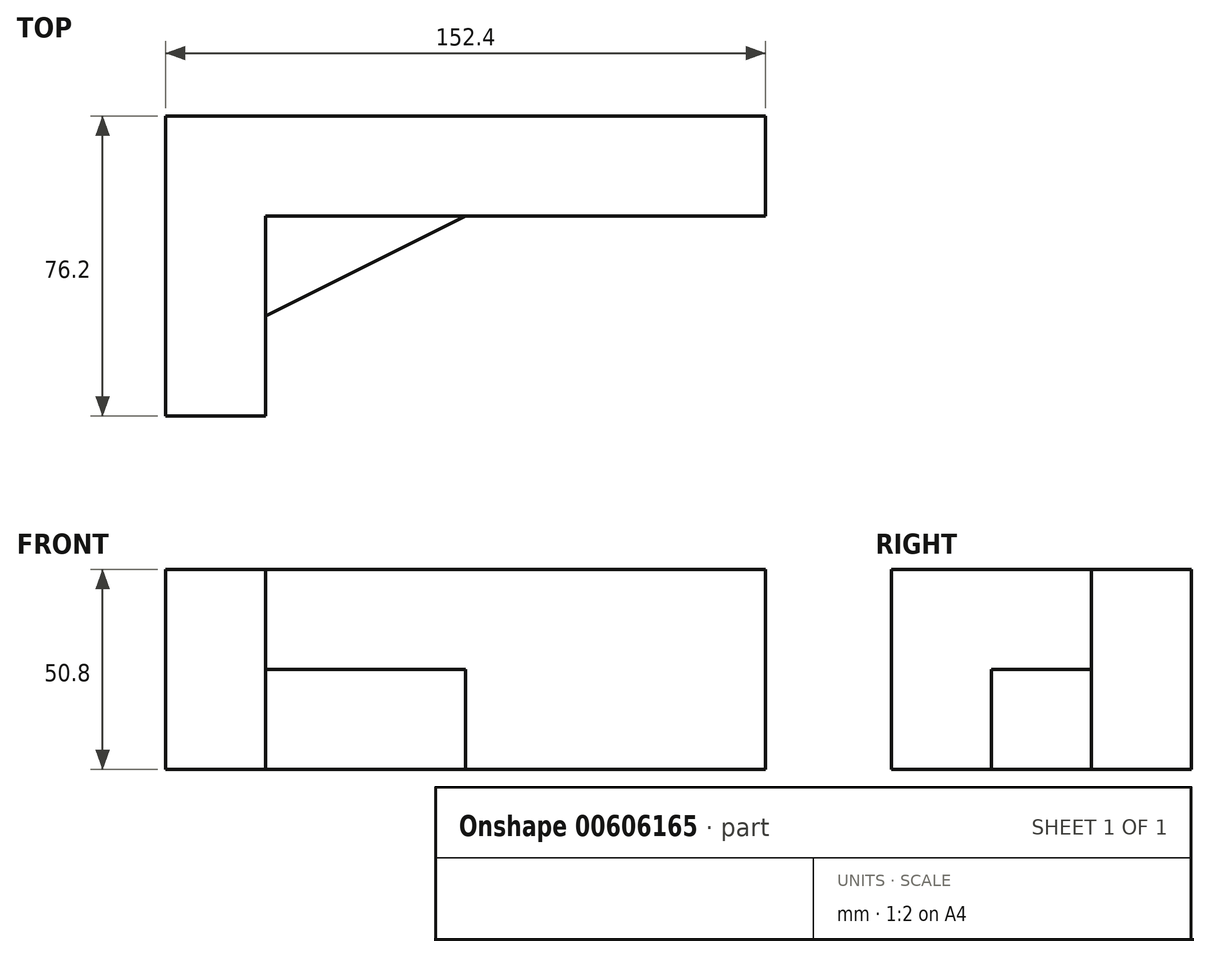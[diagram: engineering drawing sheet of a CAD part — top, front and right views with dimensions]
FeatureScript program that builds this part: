
annotation { "Feature Type Name" : "Feature", "Feature Type Description" : "" }
export const myFeature = defineFeature(function(context is Context, id is Id, definition is map)
    precondition{}
    {
        {
            var Q0;
            Q0=qCreatedBy(makeId("Top.planeOp"),FACE);
            var sketch = newSketch(context, id + "F0", { "sketchPlane" : qUnion([Q0])});
            skLineSegment(sketch, "E0", {"start": v(-46.57, 0) * mm, "end": v(-46.57, 76.2) * mm});
            skLineSegment(sketch, "E1", {"start": v(-46.57, 76.2) * mm, "end": v(105.83, 76.2) * mm});
            skLineSegment(sketch, "E2", {"start": v(105.83, 76.2) * mm, "end": v(105.83, 50.8) * mm});
            skLineSegment(sketch, "E3", {"start": v(105.83, 50.8) * mm, "end": v(-21.17, 50.8) * mm});
            skLineSegment(sketch, "E4", {"start": v(-21.17, 50.8) * mm, "end": v(-21.17, 0) * mm});
            skLineSegment(sketch, "E5", {"start": v(-21.17, 0) * mm, "end": v(-46.57, 0) * mm});
            skLineSegment(sketch, "E6", {"start": v(-21.17, 25.4) * mm, "end": v(29.63, 50.8) * mm});
            skSolve(sketch);
        }
        {
            var Q0;
            Q0=makeQuery(id+"F0.imprint","IMPRINT",FACE,{"disambiguationData":[TD([[makeQuery(id+"F0.imprint","IMPRINT",EDGE,{"derivedFrom":sQuery(id+"F0.wireOp",EDGE,"E0")}),-1.0]])]});
            extrude(context, id + "F1", {"entities" : qUnion([Q0]), "depth" : 50.8 * mm, "offsetDistance" : 25.4 * mm});
        }
        {
            var Q0;
            Q0 = qSketchRegion(id + "F0", true);
            extrude(context, id + "F2", {"entities" : qUnion([Q0]), "operationType" : NewBodyOperationType.ADD, "depth" : 25.4 * mm, "offsetDistance" : 25.4 * mm});
        }
    });
